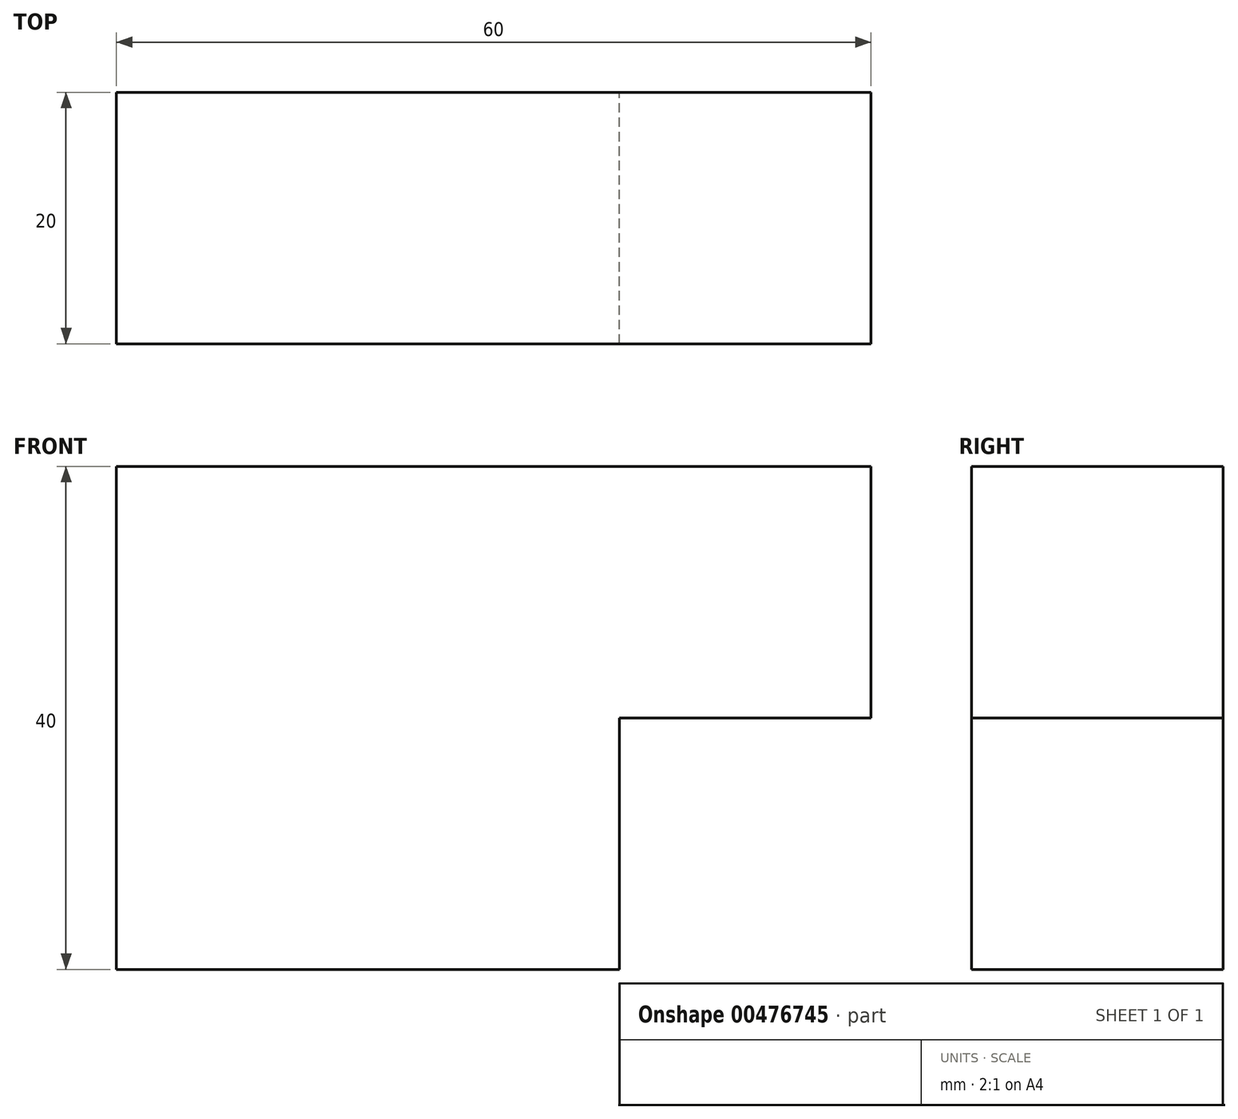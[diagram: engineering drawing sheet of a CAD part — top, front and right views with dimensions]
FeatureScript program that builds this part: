
annotation { "Feature Type Name" : "Feature", "Feature Type Description" : "" }
export const myFeature = defineFeature(function(context is Context, id is Id, definition is map)
    precondition{}
    {
        {
            var Q0;
            Q0=qCreatedBy(makeId("Front.planeOp"),FACE);
            var sketch = newSketch(context, id + "F0", { "sketchPlane" : qUnion([Q0])});
            skLineSegment(sketch, "E0", {"start": v(0, -20) * mm, "end": v(-20, -20) * mm});
            skLineSegment(sketch, "E1", {"start": v(-20, 0) * mm, "end": v(-20, -20) * mm});
            skLineSegment(sketch, "E2", {"start": v(0, -20) * mm, "end": v(20, -20) * mm});
            skLineSegment(sketch, "E3", {"start": v(20, -20) * mm, "end": v(20, 0) * mm});
            skLineSegment(sketch, "E4", {"start": v(-20, 20) * mm, "end": v(0, 20) * mm});
            skLineSegment(sketch, "E5", {"start": v(0, 20) * mm, "end": v(20, 20) * mm});
            skLineSegment(sketch, "E6", {"start": v(-20, 20) * mm, "end": v(-20, 0) * mm});
            skLineSegment(sketch, "E7", {"start": v(20, 20) * mm, "end": v(40, 20) * mm});
            skLineSegment(sketch, "E8", {"start": v(40, 20) * mm, "end": v(40, 0) * mm});
            skLineSegment(sketch, "E9", {"start": v(20, 0) * mm, "end": v(40, 0) * mm});
            skSolve(sketch);
        }
        {
            var Q0;
            Q0 = qSketchRegion(id + "F0", true);
            extrude(context, id + "F1", {"entities" : qUnion([Q0]), "depth" : 20 * mm});
        }
    });
